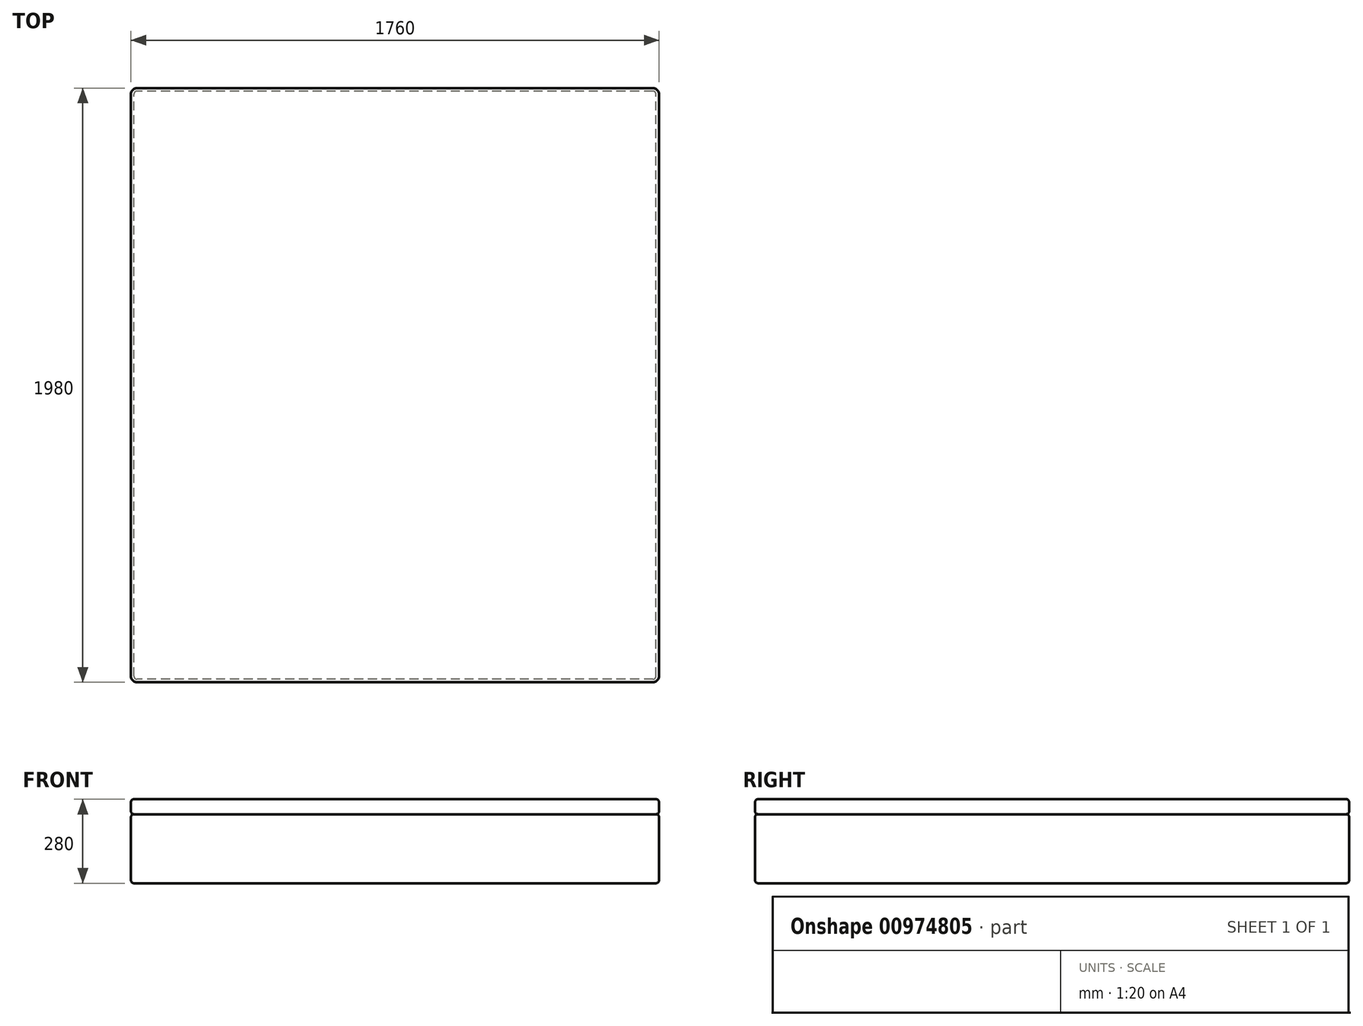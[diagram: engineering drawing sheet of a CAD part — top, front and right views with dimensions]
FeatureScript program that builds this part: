
annotation { "Feature Type Name" : "Feature", "Feature Type Description" : "" }
export const myFeature = defineFeature(function(context is Context, id is Id, definition is map)
    precondition{}
    {
        {
            var Q0;
            Q0=qCreatedBy(makeId("Top.planeOp"),FACE);
            var sketch = newSketch(context, id + "F0", { "sketchPlane" : qUnion([Q0])});
            skLineSegment(sketch, "E0.bottom", {"start": v(860, -990) * mm, "end": v(-860, -990) * mm});
            skLineSegment(sketch, "E0.top", {"start": v(860, 990) * mm, "end": v(-860, 990) * mm});
            skLineSegment(sketch, "E0.left", {"start": v(880, -970) * mm, "end": v(880, 970) * mm});
            skLineSegment(sketch, "E0.right", {"start": v(-880, -970) * mm, "end": v(-880, 970) * mm});
            skPoint(sketch, "E0.middle", {"position": v(0, 0) * mm});
            skPoint(sketch, "E1.visualSharp", {"position": v(-880, -990) * mm});
            skArc(sketch, "E1.filletArc", {"start": v(-880, -970) * mm, "mid": v(-874.14, -984.14) * mm, "end": v(-860, -990) * mm});
            skPoint(sketch, "E2.visualSharp", {"position": v(-880, 990) * mm});
            skArc(sketch, "E2.filletArc", {"start": v(-860, 990) * mm, "mid": v(-874.14, 984.14) * mm, "end": v(-880, 970) * mm});
            skPoint(sketch, "E3.visualSharp", {"position": v(880, 990) * mm});
            skArc(sketch, "E3.filletArc", {"start": v(880, 970) * mm, "mid": v(874.14, 984.14) * mm, "end": v(860, 990) * mm});
            skPoint(sketch, "E4.visualSharp", {"position": v(880, -990) * mm});
            skArc(sketch, "E4.filletArc", {"start": v(860, -990) * mm, "mid": v(874.14, -984.14) * mm, "end": v(880, -970) * mm});
            skSolve(sketch);
        }
        {
            var Q0;
            Q0 = qSketchRegion(id + "F0", true);
            extrude(context, id + "F1", {"entities" : qUnion([Q0]), "depth" : 50 * mm, "offsetDistance" : 25 * mm});
        }
        {
            var Q0;
            Q0=makeQuery(id+"F1.opExtrude","CAP_EDGE",EDGE,{"disambiguationData":[OSD([sQuery(id+"F0.wireOp",EDGE,"E0.right")])],"isStart":true});
            var Q1;
            Q1=makeQuery(id+"F1.opExtrude","CAP_EDGE",EDGE,{"disambiguationData":[OSD([sQuery(id+"F0.wireOp",EDGE,"E0.right")])],"isStart":false});
            fillet(context, id + "F2", {"entities" : qUnion([Q0, Q1]), "radius" : 10 * mm, "tangentPropagation" : true, "allowEdgeOverflow" : false});
        }
        {
            var Q0;
            Q0=makeQuery(id+"F1.opExtrude","CAP_FACE",FACE,{"disambiguationData":[OSD([sQuery(id+"F0.wireOp",EDGE,"E0.bottom"),sQuery(id+"F0.wireOp",EDGE,"E0.top"),sQuery(id+"F0.wireOp",EDGE,"E0.left"),sQuery(id+"F0.wireOp",EDGE,"E0.right"),sQuery(id+"F0.wireOp",EDGE,"E1.filletArc"),sQuery(id+"F0.wireOp",EDGE,"E2.filletArc"),sQuery(id+"F0.wireOp",EDGE,"E3.filletArc"),sQuery(id+"F0.wireOp",EDGE,"E4.filletArc")])],"isStart":true});
            var sketch = newSketch(context, id + "F3", { "sketchPlane" : qUnion([Q0])});
            skLineSegment(sketch, "E5.bottom", {"start": v(-880, 990) * mm, "end": v(880, 990) * mm});
            skLineSegment(sketch, "E5.top", {"start": v(-880, -990) * mm, "end": v(880, -990) * mm});
            skLineSegment(sketch, "E5.left", {"start": v(-880, 990) * mm, "end": v(-880, -990) * mm});
            skLineSegment(sketch, "E5.right", {"start": v(880, 990) * mm, "end": v(880, -990) * mm});
            skPoint(sketch, "E5.middle", {"position": v(0, 0) * mm});
            skSolve(sketch);
        }
        {
            var Q0;
            Q0 = qSketchRegion(id + "F3", true);
            extrude(context, id + "F4", {"entities" : qUnion([Q0]), "operationType" : NewBodyOperationType.ADD, "depth" : 230 * mm, "offsetDistance" : 25 * mm});
        }
        {
            var Q0;
            Q0=makeQuery(id+"F4.opExtrude","SWEPT_EDGE",EDGE,{"disambiguationData":[OSD([sQuery(id+"F3.wireOp",EDGE,"E5.top"),sQuery(id+"F3.wireOp",EDGE,"E5.left")])]});
            var Q1;
            Q1=makeQuery(id+"F4.opExtrude","SWEPT_EDGE",EDGE,{"disambiguationData":[OSD([sQuery(id+"F3.wireOp",EDGE,"E5.bottom"),sQuery(id+"F3.wireOp",EDGE,"E5.left")])]});
            var Q2;
            Q2=makeQuery(id+"F4.opExtrude","SWEPT_EDGE",EDGE,{"disambiguationData":[OSD([sQuery(id+"F3.wireOp",EDGE,"E5.top"),sQuery(id+"F3.wireOp",EDGE,"E5.right")])]});
            var Q3;
            Q3=makeQuery(id+"F4.opExtrude","SWEPT_EDGE",EDGE,{"disambiguationData":[OSD([sQuery(id+"F3.wireOp",EDGE,"E5.bottom"),sQuery(id+"F3.wireOp",EDGE,"E5.right")])]});
            fillet(context, id + "F5", {"entities" : qUnion([Q0, Q1, Q2, Q3]), "radius" : 20 * mm, "tangentPropagation" : true, "allowEdgeOverflow" : false});
        }
        {
            var Q0;
            Q0=makeQuery(id+"F4.opExtrude","CAP_EDGE",EDGE,{"disambiguationData":[OSD([sQuery(id+"F3.wireOp",EDGE,"E5.right")])],"isStart":true});
            var Q1;
            Q1=makeQuery(id+"F4.opExtrude","CAP_EDGE",EDGE,{"disambiguationData":[OSD([sQuery(id+"F3.wireOp",EDGE,"E5.top")])],"isStart":false});
            fillet(context, id + "F6", {"entities" : qUnion([Q0, Q1]), "radius" : 10 * mm, "tangentPropagation" : true, "allowEdgeOverflow" : false});
        }
    });
